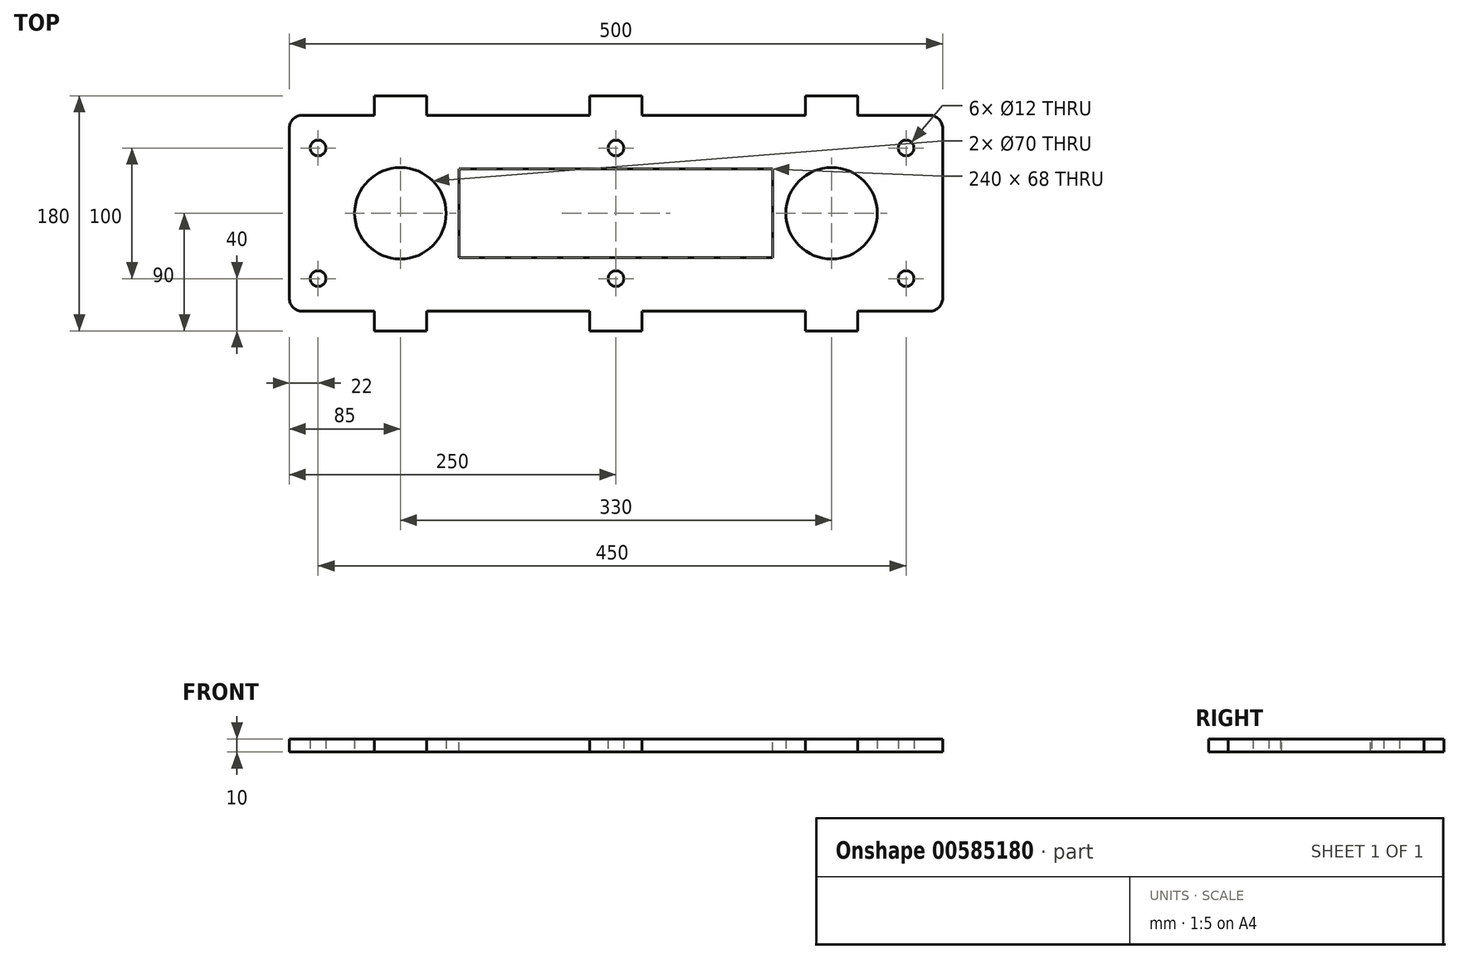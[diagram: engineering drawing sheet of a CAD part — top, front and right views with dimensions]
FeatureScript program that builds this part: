
annotation { "Feature Type Name" : "Feature", "Feature Type Description" : "" }
export const myFeature = defineFeature(function(context is Context, id is Id, definition is map)
    precondition{}
    {
        {
            var Q0;
            Q0=qCreatedBy(makeId("Top.planeOp"),FACE);
            var sketch = newSketch(context, id + "F0", { "sketchPlane" : qUnion([Q0])});
            skLineSegment(sketch, "E0.bottom", {"start": v(10, 0) * mm, "end": v(490, 0) * mm});
            skLineSegment(sketch, "E0.top", {"start": v(10, 150) * mm, "end": v(490, 150) * mm});
            skLineSegment(sketch, "E0.left", {"start": v(0, 10) * mm, "end": v(0, 140) * mm});
            skLineSegment(sketch, "E0.right", {"start": v(500, 10) * mm, "end": v(500, 140) * mm});
            skPoint(sketch, "E1.visualSharp", {"position": v(0, 150) * mm});
            skArc(sketch, "E1.filletArc", {"start": v(10, 150) * mm, "mid": v(2.93, 147.07) * mm, "end": v(0, 140) * mm});
            skPoint(sketch, "E2.visualSharp", {"position": v(500, 150) * mm});
            skArc(sketch, "E2.filletArc", {"start": v(500, 140) * mm, "mid": v(497.07, 147.07) * mm, "end": v(490, 150) * mm});
            skPoint(sketch, "E3.visualSharp", {"position": v(500, 0) * mm});
            skArc(sketch, "E3.filletArc", {"start": v(490, 0) * mm, "mid": v(497.07, 2.93) * mm, "end": v(500, 10) * mm});
            skPoint(sketch, "E4.visualSharp", {"position": v(0, 0) * mm});
            skArc(sketch, "E4.filletArc", {"start": v(0, 10) * mm, "mid": v(2.93, 2.93) * mm, "end": v(10, 0) * mm});
            skCircle(sketch, "E5", {"center": v(85, 75) * mm, "radius": 35 * mm});
            skCircle(sketch, "E6", {"center": v(415, 75) * mm, "radius": 35 * mm});
            skCircle(sketch, "E7", {"center": v(22, 125) * mm, "radius": 6 * mm});
            skCircle(sketch, "E8", {"center": v(472, 125) * mm, "radius": 6 * mm});
            skCircle(sketch, "E9", {"center": v(250, 125) * mm, "radius": 6 * mm});
            skCircle(sketch, "E10", {"center": v(472, 25) * mm, "radius": 6 * mm});
            skCircle(sketch, "E11", {"center": v(250, 25) * mm, "radius": 6 * mm});
            skCircle(sketch, "E12", {"center": v(22, 25) * mm, "radius": 6 * mm});
            skLineSegment(sketch, "E13.bottom", {"start": v(65, 0) * mm, "end": v(105, 0) * mm});
            skLineSegment(sketch, "E13.top", {"start": v(65, -15) * mm, "end": v(105, -15) * mm});
            skLineSegment(sketch, "E13.left", {"start": v(65, 0) * mm, "end": v(65, -15) * mm});
            skLineSegment(sketch, "E13.right", {"start": v(105, 0) * mm, "end": v(105, -15) * mm});
            skLineSegment(sketch, "E14.bottom", {"start": v(230, 0) * mm, "end": v(270, 0) * mm});
            skLineSegment(sketch, "E14.top", {"start": v(230, -15) * mm, "end": v(270, -15) * mm});
            skLineSegment(sketch, "E14.left", {"start": v(230, 0) * mm, "end": v(230, -15) * mm});
            skLineSegment(sketch, "E14.right", {"start": v(270, 0) * mm, "end": v(270, -15) * mm});
            skLineSegment(sketch, "E15.bottom", {"start": v(395, 0) * mm, "end": v(435, 0) * mm});
            skLineSegment(sketch, "E15.top", {"start": v(395, -15) * mm, "end": v(435, -15) * mm});
            skLineSegment(sketch, "E15.left", {"start": v(395, 0) * mm, "end": v(395, -15) * mm});
            skLineSegment(sketch, "E15.right", {"start": v(435, 0) * mm, "end": v(435, -15) * mm});
            skLineSegment(sketch, "E16.bottom", {"start": v(65, 150) * mm, "end": v(105, 150) * mm});
            skLineSegment(sketch, "E16.top", {"start": v(65, 165) * mm, "end": v(105, 165) * mm});
            skLineSegment(sketch, "E16.left", {"start": v(65, 150) * mm, "end": v(65, 165) * mm});
            skLineSegment(sketch, "E16.right", {"start": v(105, 150) * mm, "end": v(105, 165) * mm});
            skLineSegment(sketch, "E17.bottom", {"start": v(230, 150) * mm, "end": v(270, 150) * mm});
            skLineSegment(sketch, "E17.top", {"start": v(230, 165) * mm, "end": v(270, 165) * mm});
            skLineSegment(sketch, "E17.left", {"start": v(230, 150) * mm, "end": v(230, 165) * mm});
            skLineSegment(sketch, "E17.right", {"start": v(270, 150) * mm, "end": v(270, 165) * mm});
            skLineSegment(sketch, "E18.bottom", {"start": v(395, 150) * mm, "end": v(435, 150) * mm});
            skLineSegment(sketch, "E18.top", {"start": v(395, 165) * mm, "end": v(435, 165) * mm});
            skLineSegment(sketch, "E18.left", {"start": v(395, 150) * mm, "end": v(395, 165) * mm});
            skLineSegment(sketch, "E18.right", {"start": v(435, 150) * mm, "end": v(435, 165) * mm});
            skPoint(sketch, "E19", {"position": v(85, -15) * mm});
            skPoint(sketch, "E20", {"position": v(250, -15) * mm});
            skPoint(sketch, "E21", {"position": v(415, -15) * mm});
            skSolve(sketch);
        }
        {
            var Q0;
            Q0=qSketchRegion(id+"F0",true);
            extrude(context, id + "F1", {"entities" : qUnion([Q0]), "depth" : 10 * mm, "offsetDistance" : 25 * mm});
        }
        {
            var Q0;
            Q0=makeQuery(id+"F1.opExtrude","CAP_FACE",FACE,{"disambiguationData":[OSD([sQuery(id+"F0.wireOp",EDGE,"E0.bottom"),sQuery(id+"F0.wireOp",EDGE,"E0.top"),sQuery(id+"F0.wireOp",EDGE,"E0.left"),sQuery(id+"F0.wireOp",EDGE,"E0.right"),sQuery(id+"F0.wireOp",EDGE,"E1.filletArc"),sQuery(id+"F0.wireOp",EDGE,"E2.filletArc"),sQuery(id+"F0.wireOp",EDGE,"E3.filletArc"),sQuery(id+"F0.wireOp",EDGE,"E4.filletArc"),sQuery(id+"F0.wireOp",EDGE,"E5"),sQuery(id+"F0.wireOp",EDGE,"E6"),sQuery(id+"F0.wireOp",EDGE,"E7"),sQuery(id+"F0.wireOp",EDGE,"E8"),sQuery(id+"F0.wireOp",EDGE,"E9"),sQuery(id+"F0.wireOp",EDGE,"E10"),sQuery(id+"F0.wireOp",EDGE,"E11"),sQuery(id+"F0.wireOp",EDGE,"E12"),sQuery(id+"F0.wireOp",EDGE,"E13.top"),sQuery(id+"F0.wireOp",EDGE,"E13.left"),sQuery(id+"F0.wireOp",EDGE,"E13.right"),sQuery(id+"F0.wireOp",EDGE,"E14.top"),sQuery(id+"F0.wireOp",EDGE,"E14.left"),sQuery(id+"F0.wireOp",EDGE,"E14.right"),sQuery(id+"F0.wireOp",EDGE,"E15.top"),sQuery(id+"F0.wireOp",EDGE,"E15.left"),sQuery(id+"F0.wireOp",EDGE,"E15.right"),sQuery(id+"F0.wireOp",EDGE,"E16.top"),sQuery(id+"F0.wireOp",EDGE,"E16.left"),sQuery(id+"F0.wireOp",EDGE,"E16.right"),sQuery(id+"F0.wireOp",EDGE,"E17.top"),sQuery(id+"F0.wireOp",EDGE,"E17.left"),sQuery(id+"F0.wireOp",EDGE,"E17.right"),sQuery(id+"F0.wireOp",EDGE,"E18.top"),sQuery(id+"F0.wireOp",EDGE,"E18.left"),sQuery(id+"F0.wireOp",EDGE,"E18.right")])],"isStart":false});
            var sketch = newSketch(context, id + "F2", { "sketchPlane" : qUnion([Q0])});
            skLineSegment(sketch, "E22.bottom", {"start": v(130, 109) * mm, "end": v(370, 109) * mm});
            skLineSegment(sketch, "E22.top", {"start": v(130, 41) * mm, "end": v(370, 41) * mm});
            skLineSegment(sketch, "E22.left", {"start": v(130, 109) * mm, "end": v(130, 41) * mm});
            skLineSegment(sketch, "E22.right", {"start": v(370, 109) * mm, "end": v(370, 41) * mm});
            skSolve(sketch);
        }
        {
            var Q0;
            Q0 = qSketchRegion(id + "F2", true);
            extrude(context, id + "F3", {"entities" : qUnion([Q0]), "operationType" : NewBodyOperationType.REMOVE, "oppositeDirection" : true, "depth" : 25 * mm, "offsetDistance" : 25 * mm});
        }
    });
